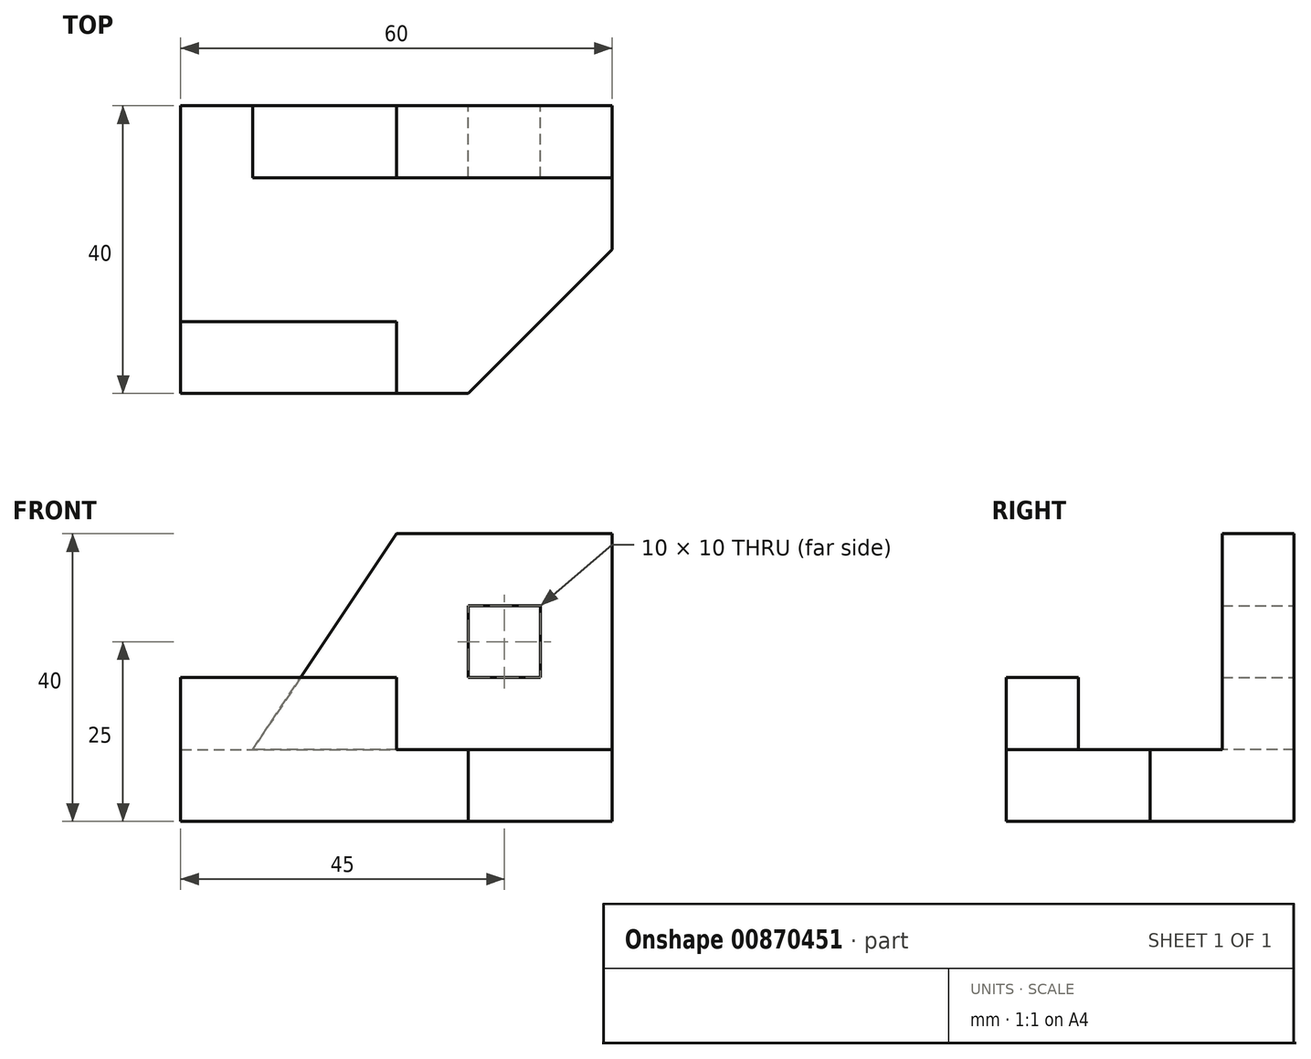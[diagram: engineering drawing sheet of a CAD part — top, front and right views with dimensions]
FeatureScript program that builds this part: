
annotation { "Feature Type Name" : "Feature", "Feature Type Description" : "" }
export const myFeature = defineFeature(function(context is Context, id is Id, definition is map)
    precondition{}
    {
        {
            var Q0;
            Q0=qCreatedBy(makeId("Top.planeOp"),FACE);
            var sketch = newSketch(context, id + "F0", { "sketchPlane" : qUnion([Q0])});
            skLineSegment(sketch, "E0.bottom", {"start": v(0, 0) * mm, "end": v(40, 0) * mm});
            skLineSegment(sketch, "E0.top", {"start": v(0, 40) * mm, "end": v(60, 40) * mm});
            skLineSegment(sketch, "E0.left", {"start": v(0, 0) * mm, "end": v(0, 40) * mm});
            skLineSegment(sketch, "E0.right", {"start": v(60, 20) * mm, "end": v(60, 40) * mm});
            skLineSegment(sketch, "E1.bottom", {"start": v(0, 0) * mm, "end": v(30, 0) * mm});
            skLineSegment(sketch, "E1.top", {"start": v(0, 10) * mm, "end": v(30, 10) * mm});
            skLineSegment(sketch, "E1.left", {"start": v(0, 0) * mm, "end": v(0, 10) * mm});
            skLineSegment(sketch, "E1.right", {"start": v(30, 0) * mm, "end": v(30, 10) * mm});
            skLineSegment(sketch, "E2.bottom", {"start": v(60, 40) * mm, "end": v(10, 40) * mm});
            skLineSegment(sketch, "E2.top", {"start": v(60, 30) * mm, "end": v(10, 30) * mm});
            skLineSegment(sketch, "E2.left", {"start": v(60, 40) * mm, "end": v(60, 30) * mm});
            skLineSegment(sketch, "E2.right", {"start": v(10, 40) * mm, "end": v(10, 30) * mm});
            skLineSegment(sketch, "E3", {"start": v(40, 0) * mm, "end": v(60, 20) * mm});
            skPoint(sketch, "E4.orphan", {"position": v(60, 0) * mm});
            skSolve(sketch);
        }
        {
            var Q0;
            {var subQ4=sQuery(id+"F0.wireOp",EDGE,"E1.top");Q0=makeQuery(id+"F0.imprint","IMPRINT",FACE,{"disambiguationData":[TD([[makeQuery(id+"F0.imprint","IMPRINT",EDGE,{"derivedFrom":subQ4}),-1.0]])]});}
            var Q1;
            {var subQ4=sQuery(id+"F0.wireOp",EDGE,"E2.top");Q1=makeQuery(id+"F0.imprint","IMPRINT",FACE,{"disambiguationData":[TD([[makeQuery(id+"F0.imprint","IMPRINT",EDGE,{"derivedFrom":subQ4}),-1.0]])]});}
            var Q2;
            {var subQ0=sQuery(id+"F0.wireOp",EDGE,"E1.top");Q2=makeQuery(id+"F0.imprint","IMPRINT",FACE,{"disambiguationData":[TD([[makeQuery(id+"F0.imprint","IMPRINT",EDGE,{"derivedFrom":subQ0}),1.0]])]});}
            extrude(context, id + "F1", {"entities" : qUnion([Q0, Q1, Q2]), "oppositeDirection" : true, "depth" : 10 * mm, "offsetDistance" : 25 * mm});
        }
        {
            var Q0;
            {var subQ4=sQuery(id+"F0.wireOp",EDGE,"E1.top");Q0=makeQuery(id+"F0.imprint","IMPRINT",FACE,{"disambiguationData":[TD([[makeQuery(id+"F0.imprint","IMPRINT",EDGE,{"derivedFrom":subQ4}),-1.0]])]});}
            extrude(context, id + "F2", {"entities" : qUnion([Q0]), "operationType" : NewBodyOperationType.ADD, "depth" : 10 * mm, "offsetDistance" : 25 * mm});
        }
        {
            var Q0;
            {var subQ4=sQuery(id+"F0.wireOp",EDGE,"E2.top");Q0=makeQuery(id+"F0.imprint","IMPRINT",FACE,{"disambiguationData":[TD([[makeQuery(id+"F0.imprint","IMPRINT",EDGE,{"derivedFrom":subQ4}),-1.0]])]});}
            extrude(context, id + "F3", {"entities" : qUnion([Q0]), "operationType" : NewBodyOperationType.ADD, "depth" : 30 * mm, "offsetDistance" : 25 * mm});
        }
        {
            var Q0;
            {var subQ0=sQuery(id+"F0.wireOp",EDGE,"E0.top");Q0=makeQuery(id+"F3.boolean.opBoolean","MERGE",FACE,{"derivedFrom":[makeQuery(id+"F1.opExtrude","SWEPT_FACE",FACE,{"disambiguationData":[OSD([subQ0])]}),makeQuery(id+"F3.opExtrude","SWEPT_FACE",FACE,{"disambiguationData":[OSD([subQ0])]})]});}
            var sketch = newSketch(context, id + "F4", { "sketchPlane" : qUnion([Q0])});
            skLineSegment(sketch, "E5.bottom", {"start": v(-50, 20) * mm, "end": v(-40, 20) * mm});
            skLineSegment(sketch, "E5.top", {"start": v(-50, 10) * mm, "end": v(-40, 10) * mm});
            skLineSegment(sketch, "E5.left", {"start": v(-50, 20) * mm, "end": v(-50, 10) * mm});
            skLineSegment(sketch, "E5.right", {"start": v(-40, 20) * mm, "end": v(-40, 10) * mm});
            skSolve(sketch);
        }
        {
            var Q0;
            Q0 = qSketchRegion(id + "F4", true);
            extrude(context, id + "F5", {"entities" : qUnion([Q0]), "operationType" : NewBodyOperationType.REMOVE, "oppositeDirection" : true, "depth" : 10 * mm, "offsetDistance" : 25 * mm});
        }
        {
            var Q0;
            Q0=makeQuery(id+"F3.opExtrude","CAP_EDGE",EDGE,{"disambiguationData":[OSD([sQuery(id+"F0.wireOp",EDGE,"E2.right")])],"isStart":false});
            chamfer(context, id + "F6", {"entities" : qUnion([Q0]), "chamferType" : ChamferType.TWO_OFFSETS, "width1" : 20 * mm, "oppositeDirection" : false, "width2" : 30 * mm, "tangentPropagation" : true});
        }
    });
